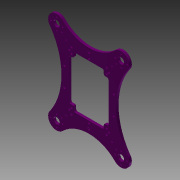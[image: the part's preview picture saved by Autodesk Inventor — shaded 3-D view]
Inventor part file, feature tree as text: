
AUTODESK INVENTOR PART (.ipt)
format: ipt  version: 2015 (Build 190159000, 159)  size: 390,144 bytes
history: native  units: mm
features: extrude x3, sketch x3
ambient origin geometry x8: Origin, YZ Plane, XZ Plane, XY Plane, X Axis, Y Axis, Z Axis, Center Point
bodies: Solid1 (feature_tree)
feature tree (6):
  extrude  "Extrusion1"  Depth=2.5mm
  extrude  "Extrusion2"  Depth=2.5mm
  extrude  "Extrusion3"  Depth=10.0mm
  sketch  "Sketch1"  dims[d2=4.625mm d3=3.5mm d4=3.5mm d10=3.5mm d15=2.5mm]
  sketch  "Sketch2"  dims[d16=2.5mm d17=2.5mm]
  sketch  "Sketch3"  dims[d18=2.5mm d20=10.0mm d21=2.5mm d22=2.5mm d23=9.0mm d26=29.0mm d30=2.0mm d31=2.0mm d34=3.5mm d35=0.0mm d40=2.5mm d41=0.0mm d42=9.0mm d43=9.0mm d44=9.0mm d45=9.0mm d46=2.5mm d50=10.0mm d51=0.0mm]
